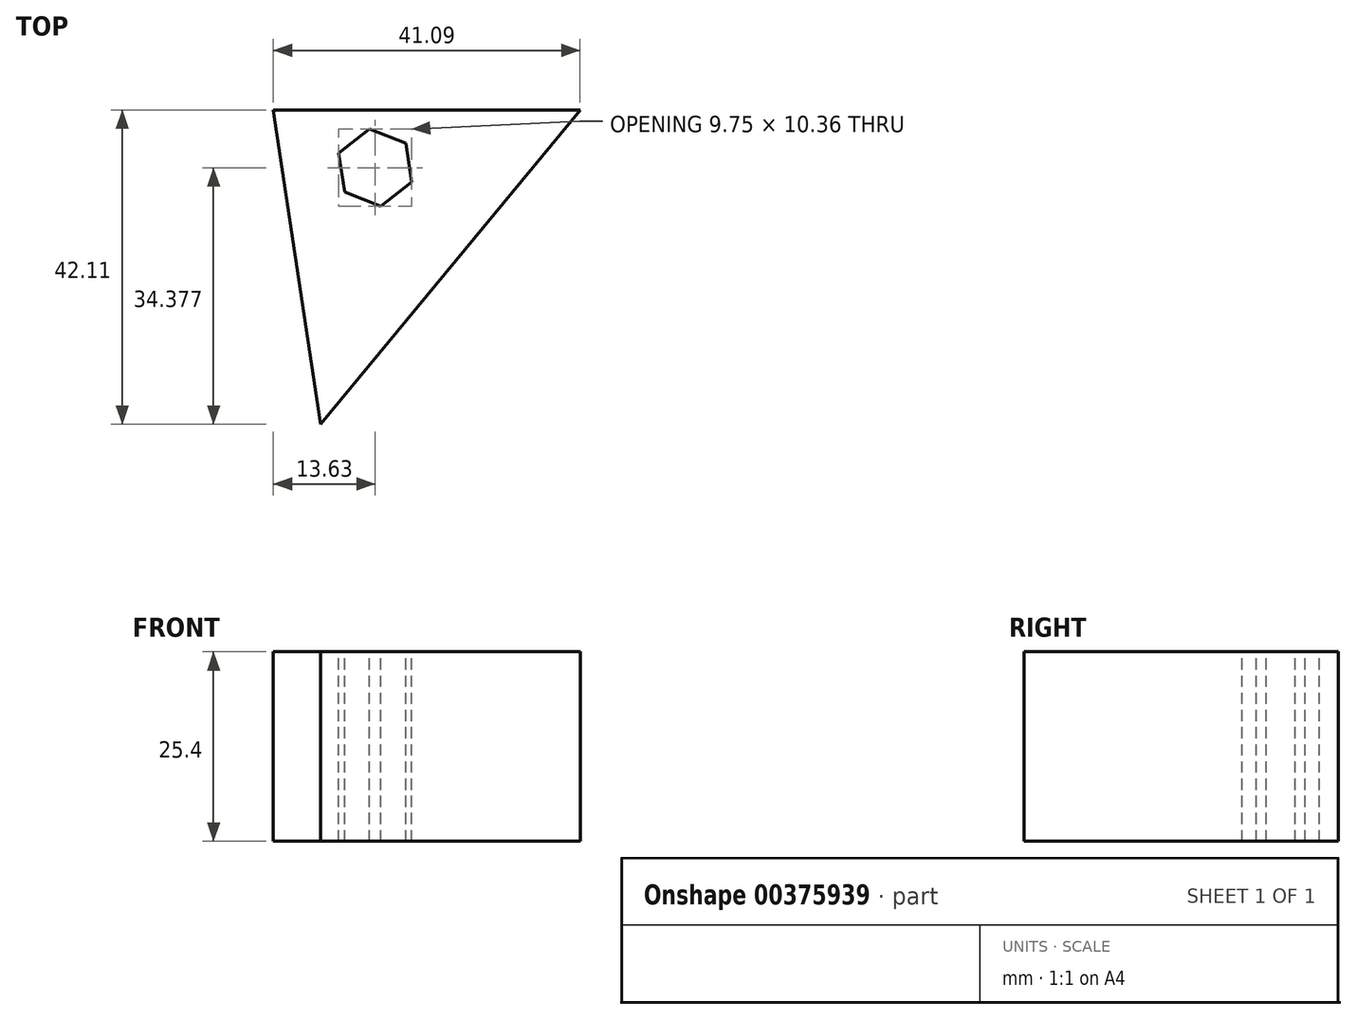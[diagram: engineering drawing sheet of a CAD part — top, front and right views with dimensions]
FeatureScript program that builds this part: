
annotation { "Feature Type Name" : "Feature", "Feature Type Description" : "" }
export const myFeature = defineFeature(function(context is Context, id is Id, definition is map)
    precondition{}
    {
        {
            var Q0;
            Q0=qCreatedBy(makeId("Top.planeOp"),FACE);
            var sketch = newSketch(context, id + "F0", { "sketchPlane" : qUnion([Q0])});
            skLineSegment(sketch, "E0", {"start": v(0, 0) * mm, "end": v(6.35, -42.11) * mm});
            skLineSegment(sketch, "E1", {"start": v(6.35, -42.11) * mm, "end": v(41.1, 0) * mm});
            skLineSegment(sketch, "E2", {"start": v(41.1, 0) * mm, "end": v(0, 0) * mm});
            skSolve(sketch);
        }
        {
            var Q0;
            Q0 = qSketchRegion(id + "F0", true);
            extrude(context, id + "F1", {"entities" : qUnion([Q0]), "depth" : 25.4 * mm});
        }
        {
            var Q0;
            Q0=makeQuery(id+"F1.opExtrude","CAP_FACE",FACE,{"disambiguationData":[OSD([sQuery(id+"F0.wireOp",EDGE,"E0"),sQuery(id+"F0.wireOp",EDGE,"E1"),sQuery(id+"F0.wireOp",EDGE,"E2")])],"isStart":false});
            var sketch = newSketch(context, id + "F2", { "sketchPlane" : qUnion([Q0])});
            skCircle(sketch, "E3.cCircle", {"center": v(13.63, -7.73) * mm, "radius": 4.54 * mm, "construction": true});
            skLineSegment(sketch, "E3.0", {"start": v(17.72, -4.47) * mm, "end": v(18.5, -9.65) * mm});
            skLineSegment(sketch, "E3.1", {"start": v(18.5, -9.65) * mm, "end": v(14.41, -12.91) * mm});
            skLineSegment(sketch, "E3.2", {"start": v(14.41, -12.91) * mm, "end": v(9.54, -11) * mm});
            skLineSegment(sketch, "E3.3", {"start": v(9.54, -11) * mm, "end": v(8.76, -5.82) * mm});
            skLineSegment(sketch, "E3.4", {"start": v(8.76, -5.82) * mm, "end": v(12.85, -2.55) * mm});
            skLineSegment(sketch, "E3.5", {"start": v(12.85, -2.55) * mm, "end": v(17.72, -4.47) * mm});
            skPoint(sketch, "E3.0.midPoint", {"position": v(18.11, -7.06) * mm});
            skSolve(sketch);
        }
        {
            var Q0;
            Q0=makeQuery(id+"F2.imprint","IMPRINT",FACE,{"disambiguationData":[TD([[makeQuery(id+"F2.imprint","IMPRINT",EDGE,{"derivedFrom":sQuery(id+"F2.wireOp",EDGE,"E3.0")}),-1.0]])]});
            extrude(context, id + "F3", {"entities" : qUnion([Q0]), "operationType" : NewBodyOperationType.REMOVE, "oppositeDirection" : true, "depth" : 25.4 * mm});
        }
    });
